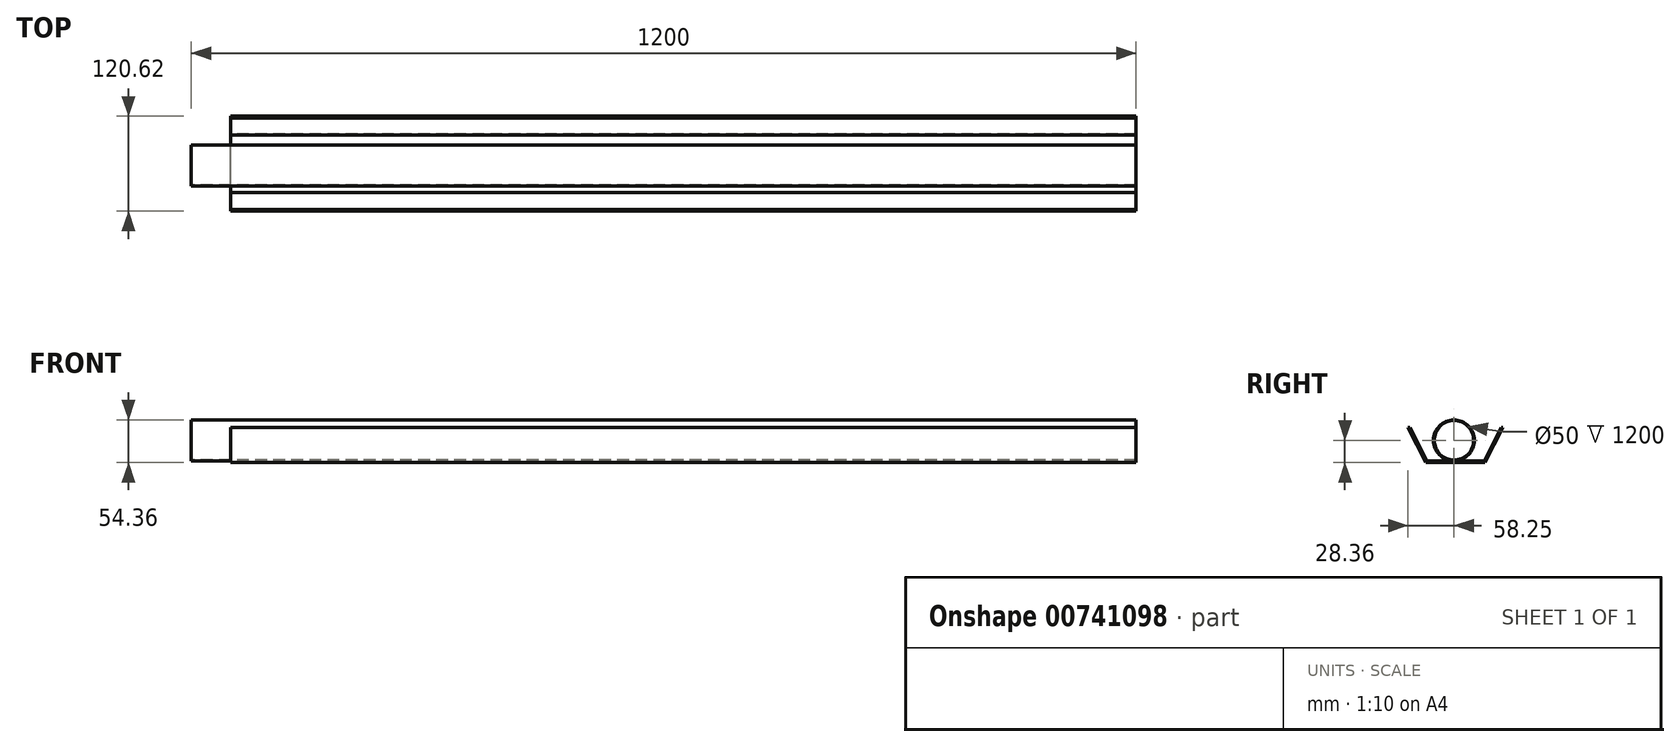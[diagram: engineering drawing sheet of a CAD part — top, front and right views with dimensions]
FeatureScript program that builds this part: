
annotation { "Feature Type Name" : "Feature", "Feature Type Description" : "" }
export const myFeature = defineFeature(function(context is Context, id is Id, definition is map)
    precondition{}
    {
        {
            var Q0;
            Q0=qCreatedBy(makeId("Right.planeOp"),FACE);
            var sketch = newSketch(context, id + "F0", { "sketchPlane" : qUnion([Q0])});
            skLineSegment(sketch, "E0", {"start": v(-35.44, -28.36) * mm, "end": v(39.56, -28.36) * mm});
            skLineSegment(sketch, "E1", {"start": v(-35.44, -28.36) * mm, "end": v(-58.25, 16.14) * mm});
            skLineSegment(sketch, "E2", {"start": v(-58.25, 16.14) * mm, "end": v(-56, 16.14) * mm});
            skLineSegment(sketch, "E3", {"start": v(62.37, 16.14) * mm, "end": v(39.56, -28.36) * mm});
            skLineSegment(sketch, "E4.0", {"start": v(-34.22, -26.36) * mm, "end": v(38.34, -26.36) * mm});
            skLineSegment(sketch, "E4.1", {"start": v(-34.22, -26.36) * mm, "end": v(-56, 16.14) * mm});
            skLineSegment(sketch, "E4.3", {"start": v(60.12, 16.14) * mm, "end": v(38.34, -26.36) * mm});
            skLineSegment(sketch, "E5.trimOffspring", {"start": v(60.12, 16.14) * mm, "end": v(62.37, 16.14) * mm});
            skSolve(sketch);
        }
        {
            var Q0;
            Q0=makeQuery(id+"F0.imprint","IMPRINT",FACE,{"disambiguationData":[TD([[makeQuery(id+"F0.imprint","IMPRINT",EDGE,{"derivedFrom":sQuery(id+"F0.wireOp",EDGE,"E0")}),1.0]])]});
            extrude(context, id + "F1", {"entities" : qUnion([Q0]), "depth" : 600 * mm, "offsetDistance" : 25 * mm, "hasSecondDirection" : true, "secondDirectionOppositeDirection" : true, "secondDirectionDepth" : 550 * mm});
        }
        {
            var Q0;
            Q0=qCreatedBy(makeId("Right.planeOp"),FACE);
            var sketch = newSketch(context, id + "F2", { "sketchPlane" : qUnion([Q0])});
            skCircle(sketch, "E6", {"center": v(0, 0) * mm, "radius": 26 * mm});
            skCircle(sketch, "E7", {"center": v(0, 0) * mm, "radius": 25 * mm});
            skSolve(sketch);
        }
        {
            var Q0;
            Q0=qSketchRegion(id+"F2",true);
            extrude(context, id + "F3", {"entities" : qUnion([Q0]), "endBound" : BoundingType.SYMMETRIC, "depth" : 1200 * mm, "offsetDistance" : 25 * mm});
        }
    });
